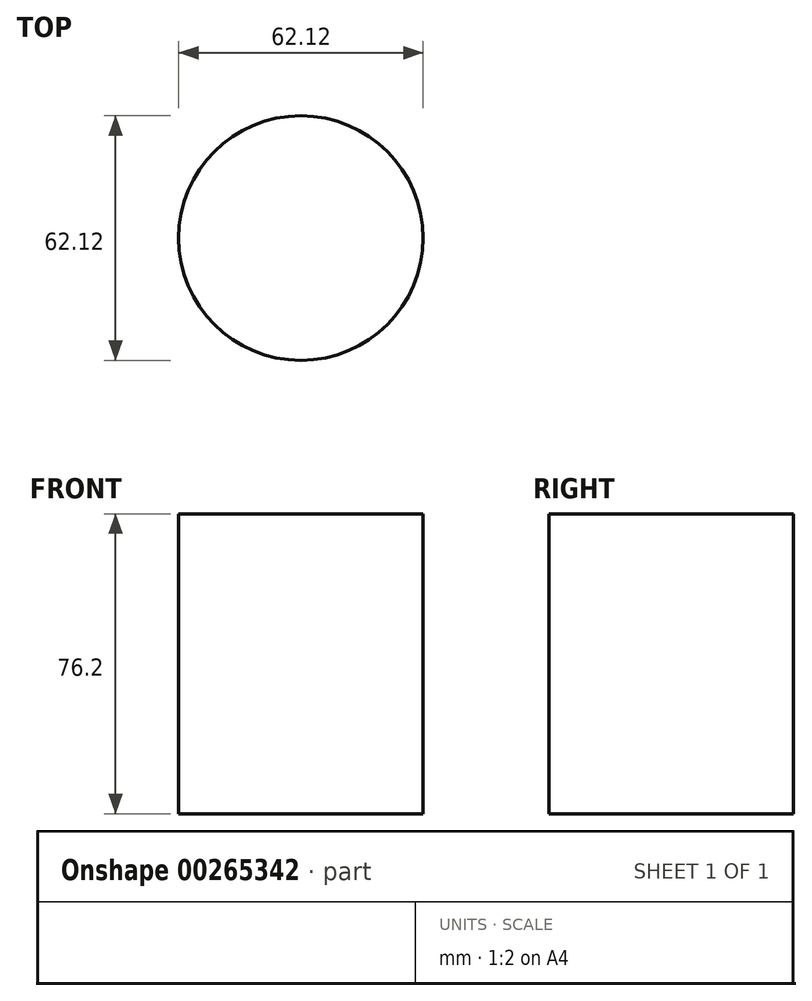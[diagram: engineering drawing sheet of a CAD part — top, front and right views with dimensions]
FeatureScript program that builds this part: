
annotation { "Feature Type Name" : "Feature", "Feature Type Description" : "" }
export const myFeature = defineFeature(function(context is Context, id is Id, definition is map)
    precondition{}
    {
        {
            var Q0;
            Q0=qCreatedBy(makeId("Top.planeOp"),FACE);
            var sketch = newSketch(context, id + "F0", { "sketchPlane" : qUnion([Q0])});
            skCircle(sketch, "E0", {"center": v(0, 0) * mm, "radius": 31.06 * mm});
            skSolve(sketch);
        }
        {
            var Q0;
            Q0=sQuery(id+"F0.wireOp",EDGE,"E0");
            extrude(context, id + "F1", {"bodyType" : ToolBodyType.SURFACE, "surfaceEntities" : qUnion([Q0]), "depth" : 76.2 * mm});
        }
    });
